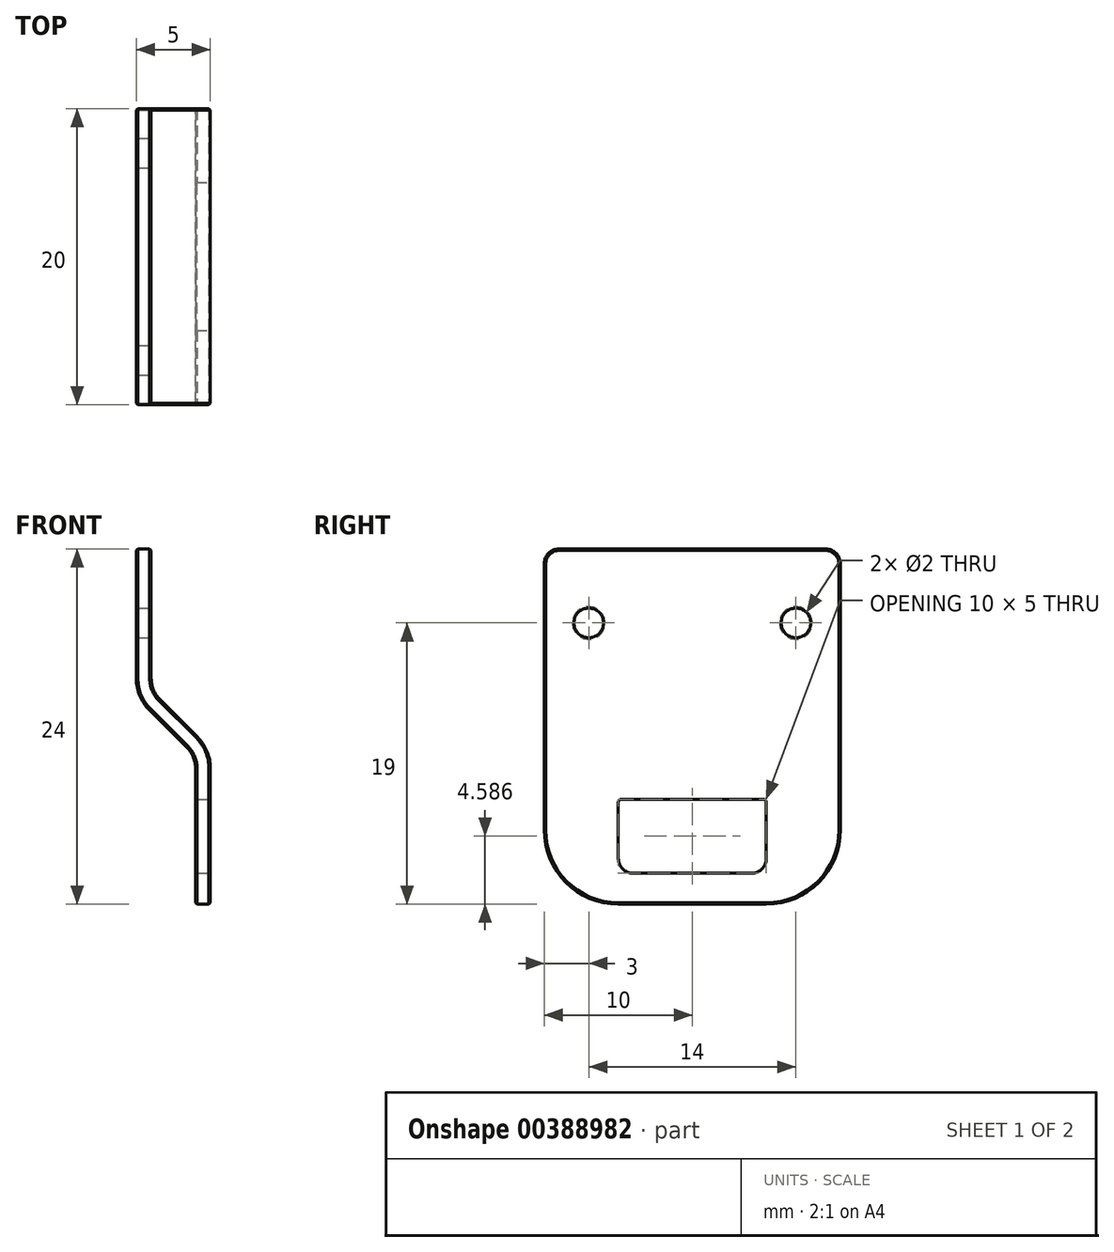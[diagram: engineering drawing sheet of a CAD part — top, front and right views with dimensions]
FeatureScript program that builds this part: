
annotation { "Feature Type Name" : "Feature", "Feature Type Description" : "" }
export const myFeature = defineFeature(function(context is Context, id is Id, definition is map)
    precondition{}
    {
        {
            var Q0;
            Q0=qCreatedBy(makeId("Front.planeOp"),FACE);
            var sketch = newSketch(context, id + "F0", { "sketchPlane" : qUnion([Q0])});
            skLineSegment(sketch, "E0", {"start": v(0, 0) * mm, "end": v(0, 9.17) * mm});
            skLineSegment(sketch, "E1", {"start": v(-0.59, 10.59) * mm, "end": v(-3.12, 13.12) * mm});
            skLineSegment(sketch, "E2", {"start": v(-4, 15.24) * mm, "end": v(-4, 24) * mm});
            skLineSegment(sketch, "E3.0", {"start": v(-3, 15.24) * mm, "end": v(-3, 24) * mm});
            skLineSegment(sketch, "E3.1", {"start": v(0.12, 11.3) * mm, "end": v(-2.41, 13.83) * mm});
            skLineSegment(sketch, "E3.2", {"start": v(1, 0) * mm, "end": v(1, 9.17) * mm});
            skLineSegment(sketch, "E4", {"start": v(-4, 24) * mm, "end": v(-3, 24) * mm});
            skLineSegment(sketch, "E5", {"start": v(0, 0) * mm, "end": v(1, 0) * mm});
            skPoint(sketch, "E6.visualSharp", {"position": v(-3, 14.41) * mm});
            skArc(sketch, "E6.filletArc", {"start": v(-3, 15.24) * mm, "mid": v(-2.85, 14.48) * mm, "end": v(-2.41, 13.83) * mm});
            skPoint(sketch, "E7.visualSharp", {"position": v(0, 10) * mm});
            skArc(sketch, "E7.filletArc", {"start": v(0, 9.17) * mm, "mid": v(-0.15, 9.94) * mm, "end": v(-0.59, 10.59) * mm});
            skPoint(sketch, "E8.visualSharp", {"position": v(-4, 14) * mm});
            skArc(sketch, "E8.filletArc", {"start": v(-4, 15.24) * mm, "mid": v(-3.77, 14.1) * mm, "end": v(-3.12, 13.12) * mm});
            skPoint(sketch, "E9.visualSharp", {"position": v(1, 10.41) * mm});
            skArc(sketch, "E9.filletArc", {"start": v(1, 9.17) * mm, "mid": v(0.77, 10.32) * mm, "end": v(0.12, 11.3) * mm});
            skSolve(sketch);
        }
        {
            var Q0;
            Q0=makeQuery(id+"F0.imprint","IMPRINT",FACE,{"disambiguationData":[TD([[makeQuery(id+"F0.imprint","IMPRINT",EDGE,{"derivedFrom":sQuery(id+"F0.wireOp",EDGE,"E0")}),-1.0]])]});
            var Q1;
            Q1=sQuery(id+"F0.wireOp",EDGE,"E4");
            extrude(context, id + "F1", {"entities" : qUnion([Q0]), "surfaceEntities" : qUnion([Q1]), "endBound" : BoundingType.SYMMETRIC, "depth" : 20 * mm});
        }
        {
            var Q0;
            Q0=makeQuery(id+"F1.opExtrude","CAP_EDGE",EDGE,{"disambiguationData":[OSD([sQuery(id+"F0.wireOp",EDGE,"E5")])],"isStart":false});
            var Q1;
            Q1=makeQuery(id+"F1.opExtrude","CAP_EDGE",EDGE,{"disambiguationData":[OSD([sQuery(id+"F0.wireOp",EDGE,"E5")])],"isStart":true});
            fillet(context, id + "F2", {"entities" : qUnion([Q0, Q1]), "radius" : 5 * mm, "tangentPropagation" : true, "allowEdgeOverflow" : false});
        }
        {
            var Q0;
            Q0=makeQuery(id+"F1.opExtrude","SWEPT_FACE",FACE,{"disambiguationData":[OSD([sQuery(id+"F0.wireOp",EDGE,"E3.0")])]});
            var sketch = newSketch(context, id + "F3", { "sketchPlane" : qUnion([Q0])});
            skLineSegment(sketch, "E10", {"start": v(0, 24) * mm, "end": v(0, 17.45) * mm, "construction": true});
            skPoint(sketch, "E10.endSnap0", {"position": v(0, 24) * mm});
            skCircle(sketch, "E11", {"center": v(-7, 19) * mm, "radius": 1 * mm});
            skCircle(sketch, "E12.MirrorC", {"center": v(7, 19) * mm, "radius": 1 * mm});
            skSolve(sketch);
        }
        {
            var Q0;
            Q0 = qSketchRegion(id + "F3", true);
            extrude(context, id + "F4", {"entities" : qUnion([Q0]), "operationType" : NewBodyOperationType.REMOVE, "oppositeDirection" : true, "depth" : 25 * mm});
        }
        {
            var Q0;
            Q0=makeQuery(id+"F1.opExtrude","CAP_EDGE",EDGE,{"disambiguationData":[OSD([sQuery(id+"F0.wireOp",EDGE,"E4")])],"isStart":false});
            var Q1;
            Q1=makeQuery(id+"F1.opExtrude","CAP_EDGE",EDGE,{"disambiguationData":[OSD([sQuery(id+"F0.wireOp",EDGE,"E4")])],"isStart":true});
            fillet(context, id + "F5", {"entities" : qUnion([Q0, Q1]), "radius" : 1 * mm, "tangentPropagation" : true, "allowEdgeOverflow" : false});
        }
        {
            var Q0;
            Q0=makeQuery(id+"F1.opExtrude","SWEPT_FACE",FACE,{"disambiguationData":[OSD([sQuery(id+"F0.wireOp",EDGE,"E3.2")])]});
            var sketch = newSketch(context, id + "F6", { "sketchPlane" : qUnion([Q0])});
            skLineSegment(sketch, "E13", {"start": v(0, 9.17) * mm, "end": v(0, 0) * mm, "construction": true});
            skLineSegment(sketch, "E14.bottom", {"start": v(4, 2.09) * mm, "end": v(-4, 2.09) * mm});
            skLineSegment(sketch, "E14.top", {"start": v(5, 7.09) * mm, "end": v(-5, 7.09) * mm});
            skLineSegment(sketch, "E14.left", {"start": v(5, 3.09) * mm, "end": v(5, 7.09) * mm});
            skLineSegment(sketch, "E14.right", {"start": v(-5, 3.09) * mm, "end": v(-5, 7.09) * mm});
            skPoint(sketch, "E14.middle", {"position": v(0, 4.59) * mm});
            skPoint(sketch, "E15.visualSharp", {"position": v(-5, 2.09) * mm});
            skArc(sketch, "E15.filletArc", {"start": v(-5, 3.09) * mm, "mid": v(-4.7, 2.38) * mm, "end": v(-4, 2.09) * mm});
            skPoint(sketch, "E16.visualSharp", {"position": v(5, 2.09) * mm});
            skArc(sketch, "E16.filletArc", {"start": v(4, 2.09) * mm, "mid": v(4.7, 2.38) * mm, "end": v(5, 3.09) * mm});
            skSolve(sketch);
        }
        {
            var Q0;
            Q0 = qSketchRegion(id + "F6", true);
            extrude(context, id + "F7", {"entities" : qUnion([Q0]), "operationType" : NewBodyOperationType.REMOVE, "endBound" : BoundingType.UP_TO_NEXT, "oppositeDirection" : true, "depth" : 25 * mm});
        }
        {
            var Q0;
            Q0=makeQuery(id+"F7.boolean.opBoolean","COPY",EDGE,{"derivedFrom":makeQuery(id+"F7.opExtrude","SWEPT_EDGE",EDGE,{"disambiguationData":[OSD([sQuery(id+"F6.wireOp",EDGE,"E14.top"),sQuery(id+"F6.wireOp",EDGE,"E14.left")])]})});
            var Q1;
            Q1=makeQuery(id+"F7.boolean.opBoolean","COPY",EDGE,{"derivedFrom":makeQuery(id+"F7.opExtrude","SWEPT_EDGE",EDGE,{"disambiguationData":[OSD([sQuery(id+"F6.wireOp",EDGE,"E14.top"),sQuery(id+"F6.wireOp",EDGE,"E14.right")])]})});
            fillet(context, id + "F8", {"entities" : qUnion([Q0, Q1]), "radius" : 0.2 * mm, "tangentPropagation" : true, "allowEdgeOverflow" : false});
        }
        {
            var Q0;
            Q0=makeQuery(id+"F2.opFillet","BLEND_EDGE",EDGE,{"blendedFrom":[makeQuery(id+"F1.opExtrude","CAP_EDGE",EDGE,{"disambiguationData":[OSD([sQuery(id+"F0.wireOp",EDGE,"E5")])],"isStart":true}),makeQuery(id+"F1.opExtrude","SWEPT_FACE",FACE,{"disambiguationData":[OSD([sQuery(id+"F0.wireOp",EDGE,"E3.2")])]})],"blendedInto":[makeQuery(id+"F1.opExtrude","SWEPT_FACE",FACE,{"disambiguationData":[OSD([sQuery(id+"F0.wireOp",EDGE,"E3.2")])]})]});
            var Q1;
            Q1=makeQuery(id+"F7.boolean.opBoolean","COPY",EDGE,{"derivedFrom":makeQuery(id+"F7.opExtrude","CAP_EDGE",EDGE,{"disambiguationData":[OSD([sQuery(id+"F6.wireOp",EDGE,"E14.top")])],"isStart":true})});
            var Q2;
            Q2=makeQuery(id+"F4.boolean.opBoolean","COPY",EDGE,{"derivedFrom":makeQuery(id+"F4.opExtrude","CAP_EDGE",EDGE,{"disambiguationData":[OSD([sQuery(id+"F3.wireOp",EDGE,"E12.MirrorC")])],"isStart":true})});
            var Q3;
            Q3=makeQuery(id+"F4.boolean.opBoolean","COPY",EDGE,{"derivedFrom":makeQuery(id+"F4.opExtrude","CAP_EDGE",EDGE,{"disambiguationData":[OSD([sQuery(id+"F3.wireOp",EDGE,"E11")])],"isStart":true})});
            var Q4;
            Q4=makeQuery(id+"F4.boolean.opBoolean","INTERSECT",EDGE,{"derivedFrom":[makeQuery(id+"F1.opExtrude","SWEPT_FACE",FACE,{"disambiguationData":[OSD([sQuery(id+"F0.wireOp",EDGE,"E2")])]}),makeQuery(id+"F4.opExtrude","SWEPT_FACE",FACE,{"disambiguationData":[OSD([sQuery(id+"F3.wireOp",EDGE,"E11")])]})]});
            var Q5;
            Q5=makeQuery(id+"F4.boolean.opBoolean","INTERSECT",EDGE,{"derivedFrom":[makeQuery(id+"F1.opExtrude","SWEPT_FACE",FACE,{"disambiguationData":[OSD([sQuery(id+"F0.wireOp",EDGE,"E2")])]}),makeQuery(id+"F4.opExtrude","SWEPT_FACE",FACE,{"disambiguationData":[OSD([sQuery(id+"F3.wireOp",EDGE,"E12.MirrorC")])]})]});
            var Q6;
            Q6=makeQuery(id+"F1.opExtrude","CAP_EDGE",EDGE,{"disambiguationData":[OSD([sQuery(id+"F0.wireOp",EDGE,"E8.filletArc")])],"isStart":false});
            var Q7;
            Q7=makeQuery(id+"F7.boolean.opBoolean","COPY",EDGE,{"derivedFrom":makeQuery(id+"F7.opExtrude","CAP_EDGE",EDGE,{"disambiguationData":[OSD([sQuery(id+"F6.wireOp",EDGE,"E14.right")])],"isStart":false})});
            chamfer(context, id + "F9", {"entities" : qUnion([Q0, Q1, Q2, Q3, Q4, Q5, Q6, Q7]), "width" : 0.1 * mm, "tangentPropagation" : true});
        }
    });
